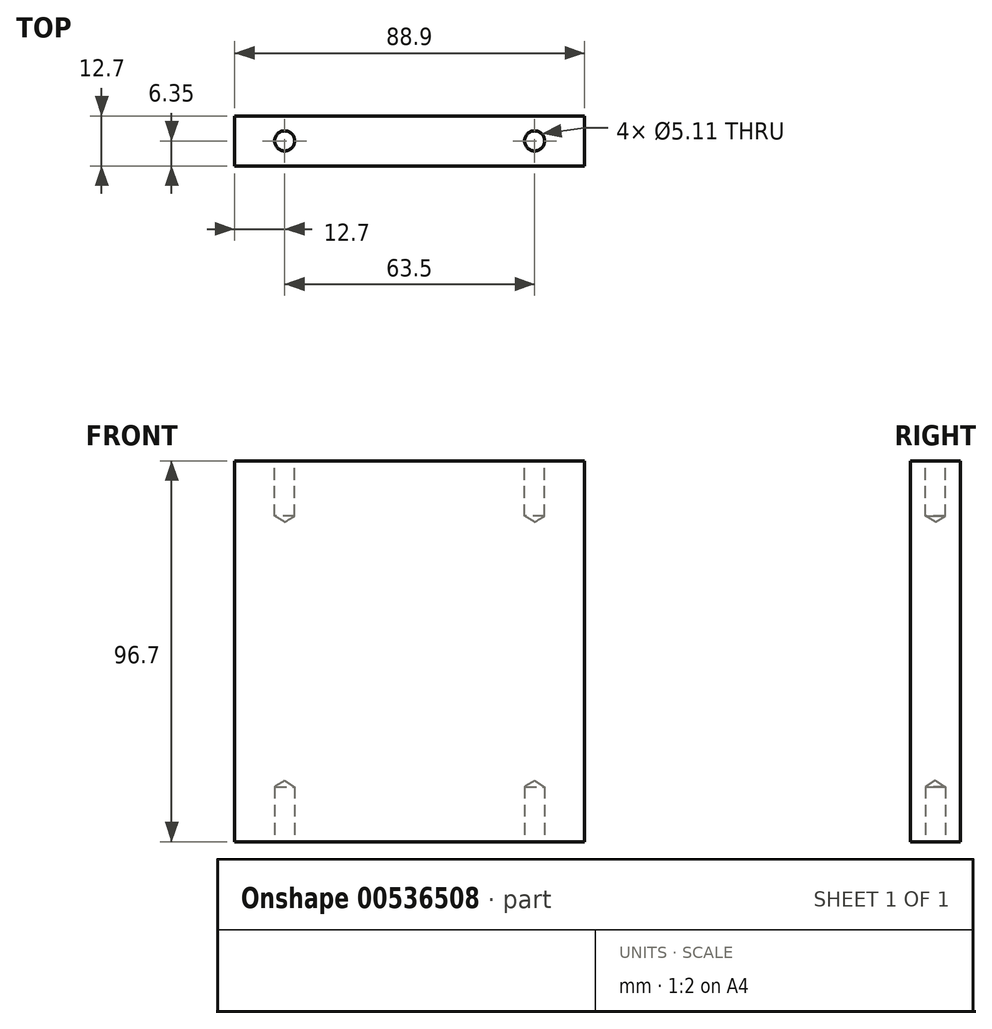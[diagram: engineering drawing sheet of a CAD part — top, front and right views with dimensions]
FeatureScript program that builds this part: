
annotation { "Feature Type Name" : "Feature", "Feature Type Description" : "" }
export const myFeature = defineFeature(function(context is Context, id is Id, definition is map)
    precondition{}
    {
        {
            var Q0;
            Q0=qCreatedBy(makeId("Top.planeOp"),FACE);
            var sketch = newSketch(context, id + "F0", { "sketchPlane" : qUnion([Q0])});
            skLineSegment(sketch, "E0.bottom", {"start": v(0, 0) * mm, "end": v(-88.9, 0) * mm});
            skLineSegment(sketch, "E0.top", {"start": v(0, 12.7) * mm, "end": v(-88.9, 12.7) * mm});
            skLineSegment(sketch, "E0.left", {"start": v(0, 0) * mm, "end": v(0, 12.7) * mm});
            skLineSegment(sketch, "E0.right", {"start": v(-88.9, 0) * mm, "end": v(-88.9, 12.7) * mm});
            skSolve(sketch);
        }
        {
            var Q0;
            Q0=makeQuery(id+"F0.imprint","IMPRINT",FACE,{"disambiguationData":[TD([[makeQuery(id+"F0.imprint","IMPRINT",EDGE,{"derivedFrom":sQuery(id+"F0.wireOp",EDGE,"E0.bottom")}),-1.0]])]});
            extrude(context, id + "F1", {"entities" : qUnion([Q0]), "depth" : 96.7 * mm, "offsetDistance" : 25.4 * mm});
        }
        {
            var Q0;
            Q0=makeQuery(id+"F1.opExtrude","CAP_FACE",FACE,{"disambiguationData":[OSD([sQuery(id+"F0.wireOp",EDGE,"E0.bottom"),sQuery(id+"F0.wireOp",EDGE,"E0.top"),sQuery(id+"F0.wireOp",EDGE,"E0.left"),sQuery(id+"F0.wireOp",EDGE,"E0.right")])],"isStart":false});
            var sketch = newSketch(context, id + "F2", { "sketchPlane" : qUnion([Q0])});
            skLineSegment(sketch, "E1", {"start": v(-88.9, 6.35) * mm, "end": v(-76.2, 6.35) * mm, "construction": true});
            skLineSegment(sketch, "E2", {"start": v(-76.2, 6.35) * mm, "end": v(-12.7, 6.35) * mm, "construction": true});
            skLineSegment(sketch, "E3", {"start": v(-12.7, 6.35) * mm, "end": v(0, 6.35) * mm, "construction": true});
            skLineSegment(sketch, "E4", {"start": v(-44.45, 6.35) * mm, "end": v(-44.45, 12.7) * mm, "construction": true});
            skSolve(sketch);
        }
        {
            var Q0;
            Q0=sQuery(id+"F2.wireOp",VERTEX,"E2.start");
            var Q1;
            Q1=sQuery(id+"F2.wireOp",VERTEX,"E3.start");
            var Q2;
            Q2=makeQuery(id+"F1.opExtrude","SWEPT_BODY",BODY,{"disambiguationData":[OSD([sQuery(id+"F0.wireOp",EDGE,"E0.bottom"),sQuery(id+"F0.wireOp",EDGE,"E0.top"),sQuery(id+"F0.wireOp",EDGE,"E0.left"),sQuery(id+"F0.wireOp",EDGE,"E0.right")])]});
            hole(context, id + "F3", {"style" : HoleStyle.SIMPLE, "endStyle" : HoleEndStyle.BLIND, "standardTappedOrClearance" : lookupTablePath({ "standard" : "ANSI", "engagement" : "75%", "pitch" : "20 tpi", "size" : "1/4", "type" : "Tapped" }), "standardBlindInLast" : lookupTablePath({ "standard" : "ANSI", "engagement" : "75%", "pitch" : "20 tpi", "size" : "1/4", "type" : "Tapped" }), "holeDiameter" : 5.1 * mm, "majorDiameter" : 6.35 * mm, "showTappedDepth" : true, "holeDepth" : 13.97 * mm, "tappedDepth" : 12.7 * mm, "tapClearance" : 1, "startFromSketch" : true, "locations" : qUnion([Q0, Q1]), "scope" : qUnion([Q2])});
        }
        {
            var Q0;
            Q0=makeQuery(id+"F1.opExtrude","CAP_FACE",FACE,{"disambiguationData":[OSD([sQuery(id+"F0.wireOp",EDGE,"E0.bottom"),sQuery(id+"F0.wireOp",EDGE,"E0.top"),sQuery(id+"F0.wireOp",EDGE,"E0.left"),sQuery(id+"F0.wireOp",EDGE,"E0.right")])],"isStart":true});
            var sketch = newSketch(context, id + "F4", { "sketchPlane" : qUnion([Q0])});
            skLineSegment(sketch, "E5", {"start": v(-88.9, -6.35) * mm, "end": v(-76.2, -6.35) * mm, "construction": true});
            skLineSegment(sketch, "E6", {"start": v(-76.2, -6.35) * mm, "end": v(-12.7, -6.35) * mm, "construction": true});
            skLineSegment(sketch, "E7", {"start": v(-12.7, -6.35) * mm, "end": v(0, -6.35) * mm, "construction": true});
            skLineSegment(sketch, "E8", {"start": v(-44.45, -6.35) * mm, "end": v(-44.45, 0) * mm, "construction": true});
            skSolve(sketch);
        }
        {
            var Q0;
            Q0=sQuery(id+"F4.wireOp",VERTEX,"E6.start");
            var Q1;
            Q1=sQuery(id+"F4.wireOp",VERTEX,"E7.start");
            var Q2;
            Q2=makeQuery(id+"F1.opExtrude","SWEPT_BODY",BODY,{"disambiguationData":[OSD([sQuery(id+"F0.wireOp",EDGE,"E0.bottom"),sQuery(id+"F0.wireOp",EDGE,"E0.top"),sQuery(id+"F0.wireOp",EDGE,"E0.left"),sQuery(id+"F0.wireOp",EDGE,"E0.right")])]});
            hole(context, id + "F5", {"style" : HoleStyle.SIMPLE, "endStyle" : HoleEndStyle.BLIND, "standardTappedOrClearance" : lookupTablePath({ "standard" : "ANSI", "engagement" : "75%", "pitch" : "20 tpi", "size" : "1/4", "type" : "Tapped" }), "standardBlindInLast" : lookupTablePath({ "standard" : "ANSI", "engagement" : "75%", "pitch" : "20 tpi", "size" : "1/4", "type" : "Tapped" }), "holeDiameter" : 5.1 * mm, "majorDiameter" : 6.35 * mm, "showTappedDepth" : true, "holeDepth" : 13.97 * mm, "tappedDepth" : 12.7 * mm, "tapClearance" : 1, "startFromSketch" : true, "locations" : qUnion([Q0, Q1]), "scope" : qUnion([Q2])});
        }
    });
